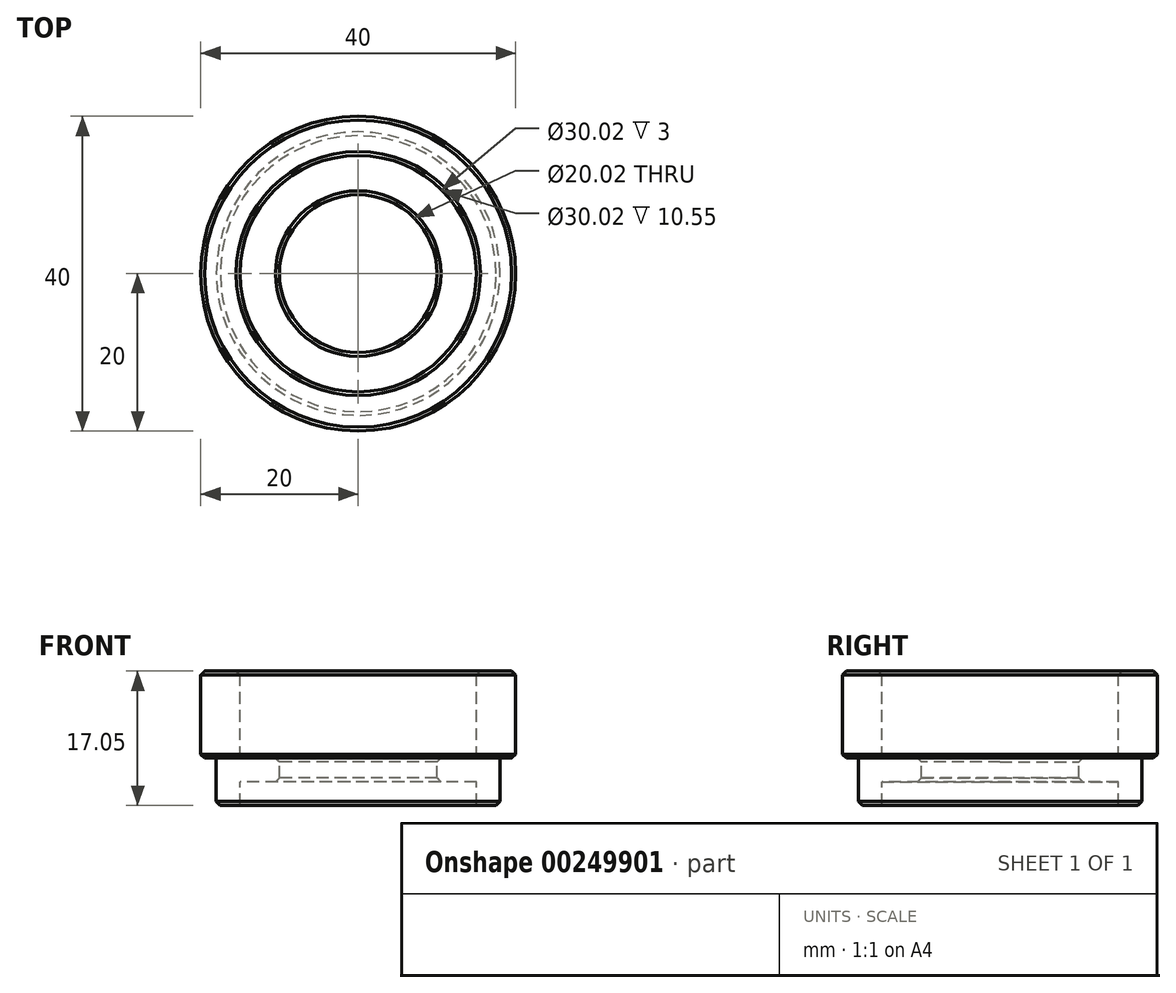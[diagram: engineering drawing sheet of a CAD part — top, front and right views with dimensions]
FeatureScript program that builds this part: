
annotation { "Feature Type Name" : "Feature", "Feature Type Description" : "" }
export const myFeature = defineFeature(function(context is Context, id is Id, definition is map)
    precondition{}
    {
        {
            var Q0;
            Q0=qCreatedBy(makeId("Front.planeOp"),FACE);
            var sketch = newSketch(context, id + "F0", { "sketchPlane" : qUnion([Q0])});
            skLineSegment(sketch, "E0", {"start": v(0, 0) * mm, "end": v(0, 11.05) * mm});
            skLineSegment(sketch, "E1", {"start": v(0, 11.05) * mm, "end": v(5, 11.05) * mm});
            skLineSegment(sketch, "E2", {"start": v(5, 11.05) * mm, "end": v(5, 0) * mm});
            skLineSegment(sketch, "E3", {"start": v(5, 0) * mm, "end": v(10, 0) * mm});
            skLineSegment(sketch, "E4", {"start": v(10, 0) * mm, "end": v(10, -3) * mm});
            skLineSegment(sketch, "E5", {"start": v(10, -3) * mm, "end": v(5, -3) * mm});
            skLineSegment(sketch, "E6", {"start": v(5, -3) * mm, "end": v(5, -6) * mm});
            skLineSegment(sketch, "E7", {"start": v(5, -6) * mm, "end": v(1.98, -6) * mm});
            skLineSegment(sketch, "E8", {"start": v(1.98, -6) * mm, "end": v(1.98, 0) * mm});
            skLineSegment(sketch, "E9", {"start": v(1.98, 0) * mm, "end": v(0, 0) * mm});
            skLineSegment(sketch, "E10", {"start": v(20, 18.48) * mm, "end": v(20, -18.42) * mm, "construction": true});
            skSolve(sketch);
        }
        {
            var Q0;
            Q0=makeQuery(id+"F0.imprint","IMPRINT",FACE,{"disambiguationData":[TD([[makeQuery(id+"F0.imprint","IMPRINT",EDGE,{"derivedFrom":sQuery(id+"F0.wireOp",EDGE,"E0")}),-1.0]])]});
            var Q1;
            Q1=sQuery(id+"F0.wireOp",EDGE,"E10");
            revolve(context, id + "F1", {"entities" : qUnion([Q0]), "axis" : qUnion([Q1]), "revolveType" : RevolveType.FULL});
        }
        {
            var Q0;
            Q0=makeQuery(id+"F1.opRevolve","SWEPT_EDGE",EDGE,{"disambiguationData":[OSD([sQuery(id+"F0.wireOp",EDGE,"E1"),sQuery(id+"F0.wireOp",EDGE,"E2")])]});
            var Q1;
            Q1=makeQuery(id+"F1.opRevolve","SWEPT_EDGE",EDGE,{"disambiguationData":[OSD([sQuery(id+"F0.wireOp",EDGE,"E0"),sQuery(id+"F0.wireOp",EDGE,"E1")])]});
            var Q2;
            Q2=makeQuery(id+"F1.opRevolve","SWEPT_EDGE",EDGE,{"disambiguationData":[OSD([sQuery(id+"F0.wireOp",EDGE,"E0"),sQuery(id+"F0.wireOp",EDGE,"E9")])]});
            var Q3;
            Q3=makeQuery(id+"F1.opRevolve","SWEPT_EDGE",EDGE,{"disambiguationData":[OSD([sQuery(id+"F0.wireOp",EDGE,"E7"),sQuery(id+"F0.wireOp",EDGE,"E8")])]});
            var Q4;
            Q4=makeQuery(id+"F1.opRevolve","SWEPT_EDGE",EDGE,{"disambiguationData":[OSD([sQuery(id+"F0.wireOp",EDGE,"E4"),sQuery(id+"F0.wireOp",EDGE,"E5")])]});
            var Q5;
            Q5=makeQuery(id+"F1.opRevolve","SWEPT_EDGE",EDGE,{"disambiguationData":[OSD([sQuery(id+"F0.wireOp",EDGE,"E3"),sQuery(id+"F0.wireOp",EDGE,"E4")])]});
            chamfer(context, id + "F2", {"entities" : qUnion([Q0, Q1, Q2, Q3, Q4, Q5]), "width" : .5 * mm, "tangentPropagation" : true});
        }
    });
